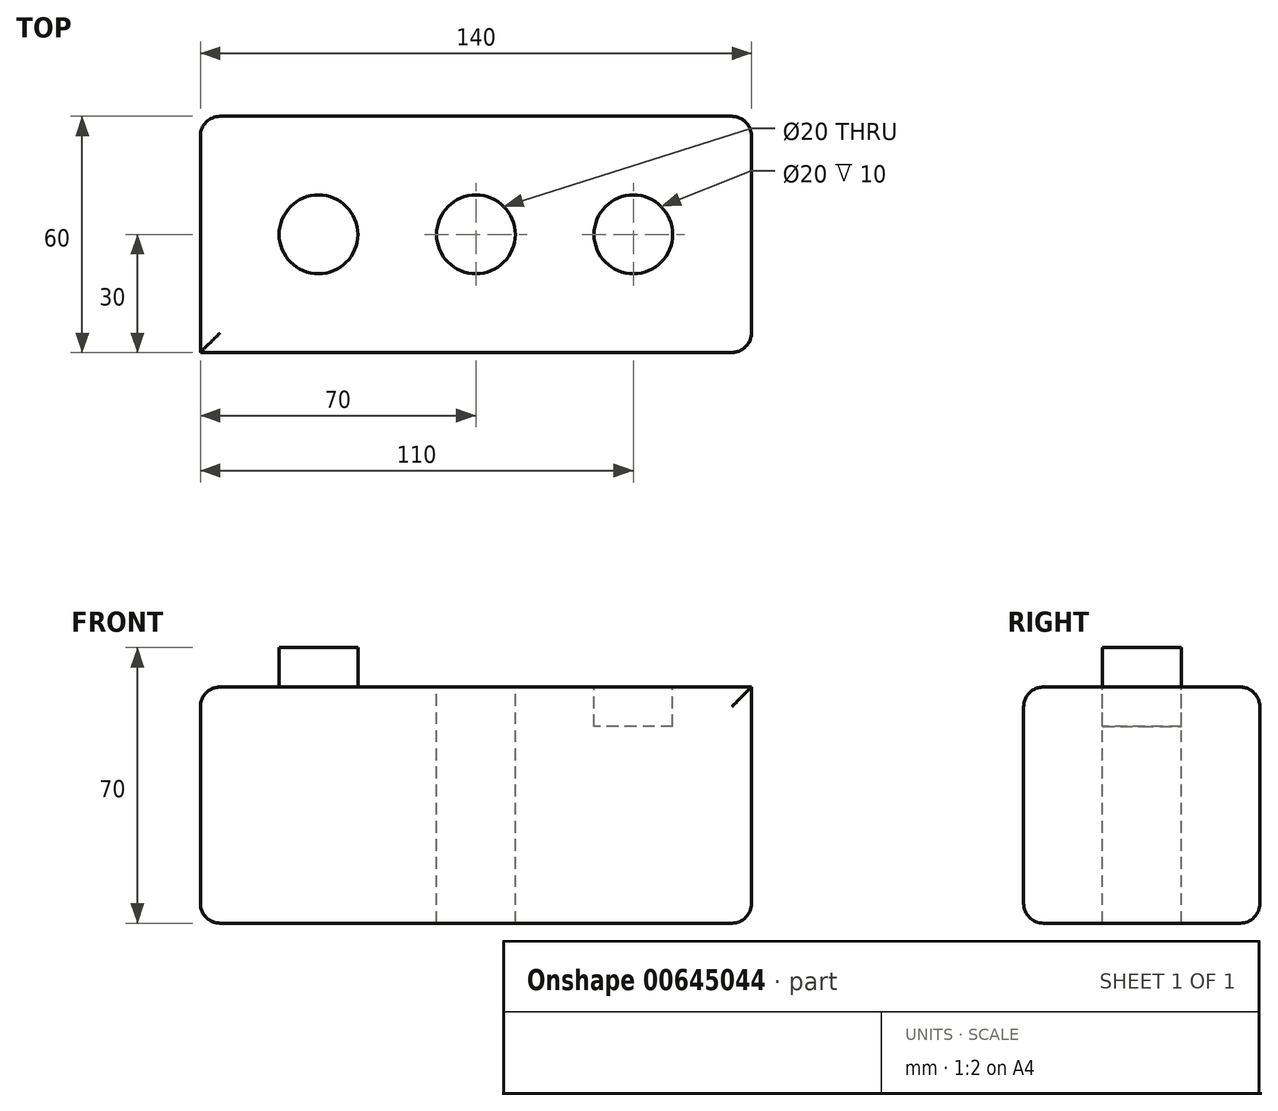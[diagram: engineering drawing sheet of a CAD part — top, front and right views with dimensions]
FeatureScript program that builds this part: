
annotation { "Feature Type Name" : "Feature", "Feature Type Description" : "" }
export const myFeature = defineFeature(function(context is Context, id is Id, definition is map)
    precondition{}
    {
        {
            var Q0;
            Q0=qCreatedBy(makeId("Top.planeOp"),FACE);
            var sketch = newSketch(context, id + "F0", { "sketchPlane" : qUnion([Q0])});
            skLineSegment(sketch, "E0.bottom", {"start": v(70, 30) * mm, "end": v(-70, 30) * mm});
            skLineSegment(sketch, "E0.top", {"start": v(70, -30) * mm, "end": v(-70, -30) * mm});
            skLineSegment(sketch, "E0.left", {"start": v(70, 30) * mm, "end": v(70, -30) * mm});
            skLineSegment(sketch, "E0.right", {"start": v(-70, 30) * mm, "end": v(-70, -30) * mm});
            skPoint(sketch, "E0.middle", {"position": v(0, 0) * mm});
            skSolve(sketch);
        }
        {
            var Q0;
            Q0 = qSketchRegion(id + "F0", true);
            extrude(context, id + "F1", {"entities" : qUnion([Q0]), "depth" : 60 * mm, "offsetDistance" : 25 * mm});
        }
        {
            var Q0;
            Q0=makeQuery(id+"F1.opExtrude","CAP_FACE",FACE,{"disambiguationData":[OSD([sQuery(id+"F0.wireOp",EDGE,"E0.bottom"),sQuery(id+"F0.wireOp",EDGE,"E0.top"),sQuery(id+"F0.wireOp",EDGE,"E0.left"),sQuery(id+"F0.wireOp",EDGE,"E0.right")])],"isStart":false});
            var sketch = newSketch(context, id + "F2", { "sketchPlane" : qUnion([Q0])});
            skCircle(sketch, "E1", {"center": v(-40, 0) * mm, "radius": 10 * mm});
            skSolve(sketch);
        }
        {
            var Q0;
            Q0=makeQuery(id+"F2.imprint","IMPRINT",FACE,{"disambiguationData":[TD([[makeQuery(id+"F2.imprint","IMPRINT",EDGE,{"derivedFrom":sQuery(id+"F2.wireOp",EDGE,"E1")}),-1.0]])]});
            var sketch = newSketch(context, id + "F3", { "sketchPlane" : qUnion([Q0])});
            skCircle(sketch, "E2", {"center": v(40, 0) * mm, "radius": 10 * mm});
            skSolve(sketch);
        }
        {
            var Q0;
            Q0=makeQuery(id+"F2.imprint","IMPRINT",FACE,{"disambiguationData":[TD([[makeQuery(id+"F2.imprint","IMPRINT",EDGE,{"derivedFrom":sQuery(id+"F2.wireOp",EDGE,"E1")}),-1.0]])]});
            var sketch = newSketch(context, id + "F4", { "sketchPlane" : qUnion([Q0])});
            skCircle(sketch, "E3", {"center": v(0, 0) * mm, "radius": 10 * mm});
            skSolve(sketch);
        }
        {
            var Q0;
            Q0 = qSketchRegion(id + "F2", true);
            extrude(context, id + "F5", {"entities" : qUnion([Q0]), "operationType" : NewBodyOperationType.ADD, "depth" : 10 * mm, "offsetDistance" : 25 * mm});
        }
        {
            var Q0;
            Q0 = qSketchRegion(id + "F4", true);
            extrude(context, id + "F6", {"entities" : qUnion([Q0]), "operationType" : NewBodyOperationType.REMOVE, "oppositeDirection" : true, "depth" : 103.2 * mm, "offsetDistance" : 25 * mm});
        }
        {
            var Q0;
            Q0 = qSketchRegion(id + "F3", true);
            extrude(context, id + "F7", {"entities" : qUnion([Q0]), "operationType" : NewBodyOperationType.REMOVE, "oppositeDirection" : true, "depth" : 10 * mm, "offsetDistance" : 25 * mm});
        }
        {
            var Q0;
            Q0=makeQuery(id+"F1.opExtrude","CAP_EDGE",EDGE,{"disambiguationData":[OSD([sQuery(id+"F0.wireOp",EDGE,"E0.bottom")])],"isStart":false});
            var Q1;
            Q1=makeQuery(id+"F1.opExtrude","CAP_EDGE",EDGE,{"disambiguationData":[OSD([sQuery(id+"F0.wireOp",EDGE,"E0.right")])],"isStart":false});
            var Q2;
            Q2=makeQuery(id+"F1.opExtrude","CAP_EDGE",EDGE,{"disambiguationData":[OSD([sQuery(id+"F0.wireOp",EDGE,"E0.top")])],"isStart":false});
            var Q3;
            Q3=makeQuery(id+"F1.opExtrude","SWEPT_FACE",FACE,{"disambiguationData":[OSD([sQuery(id+"F0.wireOp",EDGE,"E0.bottom")])]});
            var Q4;
            Q4=makeQuery(id+"F1.opExtrude","SWEPT_EDGE",EDGE,{"disambiguationData":[OSD([sQuery(id+"F0.wireOp",EDGE,"E0.bottom"),sQuery(id+"F0.wireOp",EDGE,"E0.left")])]});
            var Q5;
            Q5=makeQuery(id+"F1.opExtrude","SWEPT_EDGE",EDGE,{"disambiguationData":[OSD([sQuery(id+"F0.wireOp",EDGE,"E0.bottom"),sQuery(id+"F0.wireOp",EDGE,"E0.right")])]});
            var Q6;
            Q6=makeQuery(id+"F1.opExtrude","CAP_EDGE",EDGE,{"disambiguationData":[OSD([sQuery(id+"F0.wireOp",EDGE,"E0.left")])],"isStart":true});
            var Q7;
            Q7=makeQuery(id+"F1.opExtrude","CAP_EDGE",EDGE,{"disambiguationData":[OSD([sQuery(id+"F0.wireOp",EDGE,"E0.top")])],"isStart":true});
            var Q8;
            Q8=makeQuery(id+"F1.opExtrude","CAP_EDGE",EDGE,{"disambiguationData":[OSD([sQuery(id+"F0.wireOp",EDGE,"E0.right")])],"isStart":true});
            var Q9;
            Q9=makeQuery(id+"F1.opExtrude","SWEPT_EDGE",EDGE,{"disambiguationData":[OSD([sQuery(id+"F0.wireOp",EDGE,"E0.top"),sQuery(id+"F0.wireOp",EDGE,"E0.left")])]});
            fillet(context, id + "F8", {"entities" : qUnion([Q0, Q1, Q2, Q3, Q4, Q5, Q6, Q7, Q8, Q9]), "radius" : 5 * mm, "tangentPropagation" : true, "allowEdgeOverflow" : false});
        }
    });
